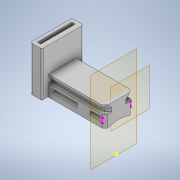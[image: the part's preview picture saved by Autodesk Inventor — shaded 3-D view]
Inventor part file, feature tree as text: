
AUTODESK INVENTOR PART (.ipt)
format: ipt  version: 2021.1 (Build 251245010, 245A)  size: 227,328 bytes
history: native  units: mm
features: move_body x4, sketch x3, extrude x2, plane x2, direct_edit x1, other x1
ambient origin geometry x8: Origin, YZ Plane, XZ Plane, XY Plane, X Axis, Y Axis, Z Axis, Center Point
bodies: Volumenkörper1 (feature_tree)
feature tree (13):
  direct_edit  "Direktbearbeitung1"
  extrude  "Extrusion1"  Depth=5.0mm TaperAngle=0.0deg
  plane  "Arbeitsebene4"
  sketch  "Skizze3"  dims[d6=0.0mm d7=0.0mm d8=-5.0mm d9=0.0mm d10=0.0mm d11=-6.75mm]
  plane  "Arbeitsebene3"
  extrude  "Extrusion2"  TaperAngle=0.0deg  [1 undecoded]
  sketch  "Skizze1"  dims[d0=0.0mm d1=0.0mm d2=15.75mm d3=5.0mm d4=0.0mm d5=0.0mm]
  sketch  "Skizze5"  dims[d12=10.0mm d13=0.0mm d16=5.5mm d17=0.0mm]
  other  "Körper1"
  move_body  "Verschieben1"
  move_body  "Verschieben2"
  move_body  "Verschieben3"
  move_body  "Verschieben4"
note: 1 required parameter value undecoded (feature->parameter linkage not recoverable at this tier; creation-order binding heuristic only, values carry confidence <= 0.55)
